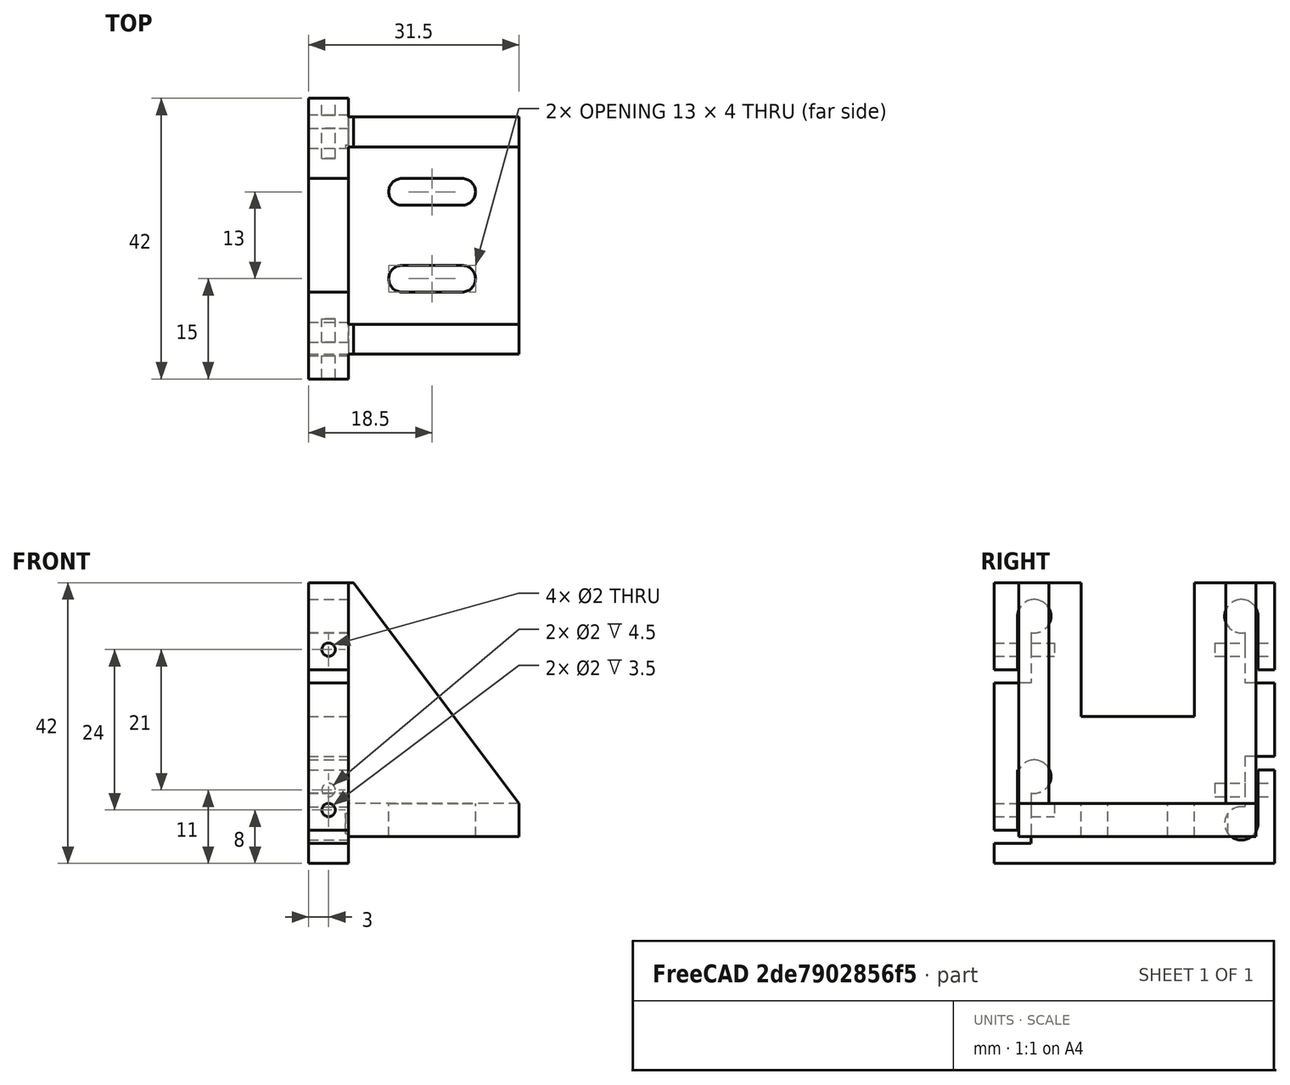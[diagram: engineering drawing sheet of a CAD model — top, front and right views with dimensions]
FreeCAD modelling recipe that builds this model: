
FCSTD DOCUMENT  (FreeCAD 0.18R16110 (Git))
Label: slider-side-wall-right
License: All rights reserved
LicenseURL: http://en.wikipedia.org/wiki/All_rights_reserved
objects: Part::Cut×20, Part::Box×13, Part::Cylinder×10, Part::MultiFuse×3, Part::Wedge×2, Mesh::Feature×1
note: 48 computed .brp shape members not serialized (recipe doc carries the construction recipe); baked Part::Feature solids carry a one-line shape summary decoded from their .brp

FEATURE [Part::Wedge] Wedge  label="Keil"
  AttacherType = Attacher::AttachEngine3D
  Placement = pos=(-29,2.8,44.5) rot=(-1,0,0;1.5708rad)
  X2max = 39
  X2min = 0
  Xmax = 5
  Xmin = 0
  Ymax = 25.5
  Ymin = 0
  Z2max = 4.5
  Z2min = 0
  Zmax = 4.5
  Zmin = 0
FEATURE [Part::Wedge] Wedge001  label="Keil001"
  AttacherType = Attacher::AttachEngine3D
  Placement = pos=(-29,33.8,44.5) rot=(-1,0,0;1.5708rad)
  X2max = 39
  X2min = 0
  Xmax = 5
  Xmin = 0
  Ymax = 25.5
  Ymin = 0
  Z2max = 4.5
  Z2min = 0
  Zmax = 4.5
  Zmin = 0
FEATURE [Part::Box] Box026  label="Quader020"
  AttacherType = Attacher::AttachEngine3D
  Height = 10
  Length = 2
  Placement = pos=(-19,-6,11) rot=(0,0,1;0rad)
  Width = 10
FEATURE [Part::Cylinder] Cylinder104  label="Führung_re005"
  Angle = 360
  AttacherType = Attacher::AttachEngine3D
  Height = 8
  Placement = pos=(4,5,12) rot=(1,0,0;0rad)
  Radius = 2.5
FEATURE [Part::Box] Box029  label="Quader023"
  AttacherType = Attacher::AttachEngine3D
  Height = 10
  Length = 10
  Placement = pos=(-6,2.5,12) rot=(0,0,1;0rad)
  Width = 2
FEATURE [Part::Box] Box037  label="Quader031"
  AttacherType = Attacher::AttachEngine3D
  Height = 26
  Length = 5
  Placement = pos=(-29,7,18.5) rot=(0,0,1;0rad)
  Width = 27
FEATURE [Part::Cylinder] Cylinder102  label="Führung_li004"
  Angle = 360
  AttacherType = Attacher::AttachEngine3D
  Height = 8
  Placement = pos=(-20,36,12) rot=(1,0,0;0rad)
  Radius = 2.5
FEATURE [Part::Box] Box030  label="Quader024"
  AttacherType = Attacher::AttachEngine3D
  Height = 10
  Length = 10
  Placement = pos=(-6,36.5,11) rot=(0,0,1;0rad)
  Width = 2
FEATURE [Part::Cylinder] Cylinder103  label="Führung_re004"
  Angle = 360
  AttacherType = Attacher::AttachEngine3D
  Height = 8
  Placement = pos=(-27,5,12) rot=(1,0,0;0rad)
  Radius = 2.5
FEATURE [Part::Box] Box033  label="Quader027"
  AttacherType = Attacher::AttachEngine3D
  Height = 10
  Length = 10
  Placement = pos=(-29,36.5,12) rot=(0,0,1;0rad)
  Width = 2
FEATURE [Part::Cylinder] Cylinder116  label="Zylinder089"
  Angle = 360
  AttacherType = Attacher::AttachEngine3D
  Height = 10
  Placement = pos=(-31,16,36) rot=(0,1,0;1.5708rad)
  Radius = 2
FEATURE [Part::Box] Box038  label="Quader032"
  AttacherType = Attacher::AttachEngine3D
  Height = 9
  Length = 10
  Placement = pos=(-31,14,27) rot=(0,0,1;0rad)
  Width = 4
FEATURE [Part::Cylinder] Cylinder105  label="Führung_li005"
  Angle = 360
  AttacherType = Attacher::AttachEngine3D
  Height = 8
  Placement = pos=(4,36,12) rot=(1,0,0;0rad)
  Radius = 2.5
FEATURE [Part::Box] Box039  label="Quader033"
  AttacherType = Attacher::AttachEngine3D
  Height = 10
  Length = 4
  Placement = pos=(9,-1,11) rot=(0,0,1;0rad)
  Width = 44
FEATURE [Part::Cylinder] Cylinder114  label="Zylinder087"
  Angle = 360
  AttacherType = Attacher::AttachEngine3D
  Height = 10
  Placement = pos=(-31,16,27) rot=(0,1,0;1.5708rad)
  Radius = 2
FEATURE [Part::MultiFuse] Fusion014
  Placement = pos=(0,-2,0) rot=(0,0,1;0rad)
  Shapes = -> [Box038,Cylinder116,Cylinder114]
FEATURE [Part::MultiFuse] Fusion015
  Placement = pos=(0,11,0) rot=(0,0,1;0rad)
  Shapes = -> [Box038,Cylinder116,Cylinder114]
FEATURE [Part::Cylinder] Cylinder094  label="Zylinder078"
  Angle = 360
  AttacherType = Attacher::AttachEngine3D
  Height = 9
  Placement = pos=(-1,9,16) rot=(1,0,0;1.5708rad)
  Radius = 1
FEATURE [Part::Box] Box007  label="Quader006"
  AttacherType = Attacher::AttachEngine3D
  Height = 42
  Length = 43
  Placement = pos=(-33,42,13) rot=(1,0,0;1.5708rad)
  Width = 6
FEATURE [Part::Box] Box032  label="Quader026"
  AttacherType = Attacher::AttachEngine3D
  Height = 10
  Length = 2
  Placement = pos=(-30,36.5,11) rot=(0,0,1;0rad)
  Width = 10
FEATURE [Part::Cylinder] Cylinder097  label="Zylinder081"
  Angle = 360
  AttacherType = Attacher::AttachEngine3D
  Height = 9
  Placement = pos=(-25,42,16) rot=(1,0,0;1.5708rad)
  Radius = 1
FEATURE [Part::Box] Box015  label="Quader009"
  AttacherType = Attacher::AttachEngine3D
  Height = 10
  Length = 22
  Placement = pos=(-11,12,12) rot=(0,0,1;0rad)
  Width = 17
FEATURE [Part::Cylinder] Cylinder096  label="Zylinder080"
  Angle = 360
  AttacherType = Attacher::AttachEngine3D
  Height = 9
  Placement = pos=(-22,9,16) rot=(1,0,0;1.5708rad)
  Radius = 1
FEATURE [Part::Box] Box028  label="Quader022"
  AttacherType = Attacher::AttachEngine3D
  Height = 10
  Length = 2
  Placement = pos=(-6,-6,12) rot=(0,0,1;0rad)
  Width = 10
FEATURE [Part::Box] Box031  label="Quader025"
  AttacherType = Attacher::AttachEngine3D
  Height = 10
  Length = 2
  Placement = pos=(-6,37,11) rot=(0,0,1;0rad)
  Width = 10
FEATURE [Part::Box] Box027  label="Quader021"
  AttacherType = Attacher::AttachEngine3D
  Height = 10
  Length = 10
  Placement = pos=(-27,2.5,11) rot=(0,0,1;0rad)
  Width = 2
FEATURE [Part::Cylinder] Cylinder095  label="Zylinder079"
  Angle = 360
  AttacherType = Attacher::AttachEngine3D
  Height = 9
  Placement = pos=(-1,42,16) rot=(1,0,0;1.5708rad)
  Radius = 1
FEATURE [Part::Cut] Cut097
  Base = -> Box007
  Tool = -> Box015
FEATURE [Part::Cut] Cut117
  Base = -> Cut097
  Tool = -> Box026
FEATURE [Part::Cut] Cut118
  Base = -> Cut117
  Tool = -> Box033
FEATURE [Part::Cut] Cut119
  Base = -> Cut118
  Tool = -> Box032
FEATURE [Part::Cut] Cut120
  Base = -> Cut119
  Tool = -> Box031
FEATURE [Part::Cut] Cut121
  Base = -> Cut120
  Tool = -> Box030
FEATURE [Part::Cut] Cut122
  Base = -> Cut121
  Tool = -> Box029
FEATURE [Part::Cut] Cut123
  Base = -> Cut122
  Tool = -> Box028
FEATURE [Part::Cut] Cut124
  Base = -> Cut123
  Tool = -> Box027
FEATURE [Part::Cut] Cut125
  Base = -> Cut124
  Tool = -> Cylinder094
FEATURE [Part::Cut] Cut126
  Base = -> Cut125
  Tool = -> Cylinder095
FEATURE [Part::Cut] Cut127
  Base = -> Cut126
  Tool = -> Cylinder096
FEATURE [Part::Cut] Cut128
  Base = -> Cut127
  Tool = -> Cylinder097
FEATURE [Part::Cut] Cut129
  Base = -> Cut128
  Tool = -> Cylinder102
FEATURE [Part::Cut] Cut130
  Base = -> Cut129
  Tool = -> Cylinder103
FEATURE [Part::Cut] Cut131
  Base = -> Cut130
  Tool = -> Cylinder104
FEATURE [Part::Cut] Cut132  label="Wange001"
  Base = -> Cut131
  Tool = -> Cylinder105
FEATURE [Part::Cut] Cut144
  Base = -> Box037
  Tool = -> Fusion014
FEATURE [Part::Cut] Cut145
  Base = -> Cut144
  Tool = -> Fusion015
FEATURE [Part::MultiFuse] Fusion016  label="Wange002"
  Shapes = -> [Cut132,Wedge,Wedge001,Cut145]
FEATURE [Part::Cut] Cut146  label="slider-side-wall-right"
  Base = -> Fusion016
  Placement = pos=(-104,140,0) rot=(0.707107,0,0.707107;3.14159rad)
  Tool = -> Box039
FEATURE [Mesh::Feature] Mesh  label="slider-side-wall-right (Meshed)"
